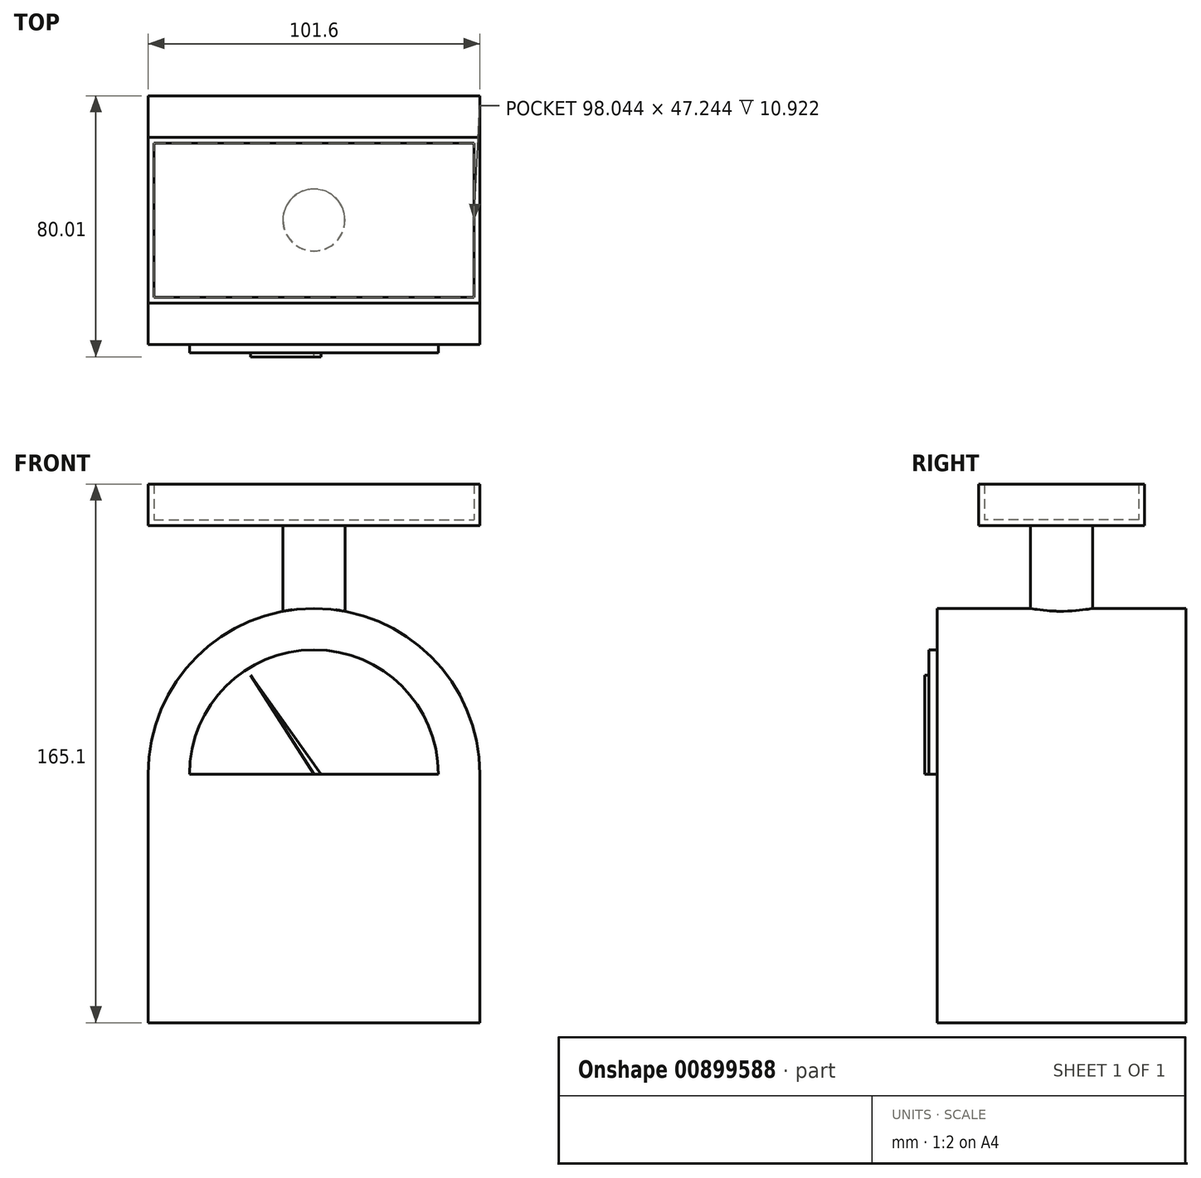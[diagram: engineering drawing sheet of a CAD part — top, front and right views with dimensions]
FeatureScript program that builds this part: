
annotation { "Feature Type Name" : "Feature", "Feature Type Description" : "" }
export const myFeature = defineFeature(function(context is Context, id is Id, definition is map)
    precondition{}
    {
        {
            var Q0;
            Q0=qCreatedBy(makeId("Front.planeOp"),FACE);
            var sketch = newSketch(context, id + "F0", { "sketchPlane" : qUnion([Q0])});
            skLineSegment(sketch, "E0", {"start": v(-50.8, 0) * mm, "end": v(50.8, 0) * mm});
            skLineSegment(sketch, "E1", {"start": v(50.8, 0) * mm, "end": v(50.8, 76.2) * mm});
            skLineSegment(sketch, "E2", {"start": v(-50.8, 0) * mm, "end": v(-50.8, 76.2) * mm});
            skArc(sketch, "E3", {"start": v(50.8, 76.2) * mm, "mid": v(0, 127) * mm, "end": v(-50.8, 76.2) * mm});
            skSolve(sketch);
        }
        {
            var Q0;
            Q0=makeQuery(id+"F0.imprint","IMPRINT",FACE,{"disambiguationData":[TD([[makeQuery(id+"F0.imprint","IMPRINT",EDGE,{"derivedFrom":sQuery(id+"F0.wireOp",EDGE,"E0")}),1.0]])]});
            extrude(context, id + "F1", {"entities" : qUnion([Q0]), "depth" : 76.2 * mm, "offsetDistance" : 25.4 * mm});
        }
        {
            var Q0;
            Q0=makeQuery(id+"F1.opExtrude","CAP_FACE",FACE,{"disambiguationData":[OSD([sQuery(id+"F0.wireOp",EDGE,"E0"),sQuery(id+"F0.wireOp",EDGE,"E1"),sQuery(id+"F0.wireOp",EDGE,"E2"),sQuery(id+"F0.wireOp",EDGE,"E3")])],"isStart":false});
            var sketch = newSketch(context, id + "F2", { "sketchPlane" : qUnion([Q0])});
            skLineSegment(sketch, "E4", {"start": v(-38.1, 76.2) * mm, "end": v(38.1, 76.2) * mm});
            skArc(sketch, "E5", {"start": v(38.1, 76.2) * mm, "mid": v(0, 114.3) * mm, "end": v(-38.1, 76.2) * mm});
            skSolve(sketch);
        }
        {
            var Q0;
            Q0=makeQuery(id+"F2.imprint","IMPRINT",FACE,{"disambiguationData":[TD([[makeQuery(id+"F2.imprint","IMPRINT",EDGE,{"derivedFrom":sQuery(id+"F2.wireOp",EDGE,"E4")}),1.0]])]});
            extrude(context, id + "F3", {"entities" : qUnion([Q0]), "depth" : 2.54 * mm, "offsetDistance" : 25.4 * mm});
        }
        {
            var Q0;
            Q0=makeQuery(id+"F3.opExtrude","CAP_FACE",FACE,{"disambiguationData":[OSD([sQuery(id+"F2.wireOp",EDGE,"E4"),sQuery(id+"F2.wireOp",EDGE,"E5")])],"isStart":false});
            var sketch = newSketch(context, id + "F4", { "sketchPlane" : qUnion([Q0])});
            skLineSegment(sketch, "E6", {"start": v(0, 76.2) * mm, "end": v(-19.35, 106.48) * mm});
            skLineSegment(sketch, "E7", {"start": v(-19.35, 106.48) * mm, "end": v(2.15, 76.2) * mm});
            skLineSegment(sketch, "E8", {"start": v(2.15, 76.2) * mm, "end": v(0, 76.2) * mm});
            skSolve(sketch);
        }
        {
            var Q0;
            Q0=makeQuery(id+"F4.imprint","IMPRINT",FACE,{"disambiguationData":[TD([[makeQuery(id+"F4.imprint","IMPRINT",EDGE,{"derivedFrom":sQuery(id+"F4.wireOp",EDGE,"E6")}),-1.0]])]});
            extrude(context, id + "F5", {"entities" : qUnion([Q0]), "depth" : 1.27 * mm, "offsetDistance" : 25.4 * mm});
        }
        {
            var Q0;
            Q0=qCreatedBy(makeId("Top.planeOp"),FACE);
            var sketch = newSketch(context, id + "F6", { "sketchPlane" : qUnion([Q0])});
            skCircle(sketch, "E9", {"center": v(0, -38.1) * mm, "radius": 9.53 * mm});
            skSolve(sketch);
        }
        {
            var Q0;
            Q0=makeQuery(id+"F6.imprint","IMPRINT",FACE,{"disambiguationData":[TD([[makeQuery(id+"F6.imprint","IMPRINT",EDGE,{"derivedFrom":sQuery(id+"F6.wireOp",EDGE,"E9")}),1.0]])]});
            extrude(context, id + "F7", {"entities" : qUnion([Q0]), "operationType" : NewBodyOperationType.ADD, "depth" : 152.4 * mm, "offsetDistance" : 25.4 * mm});
        }
        {
            var Q0;
            Q0=makeQuery(id+"F7.opExtrude","CAP_FACE",FACE,{"disambiguationData":[OSD([sQuery(id+"F6.wireOp",EDGE,"E9")])],"isStart":false});
            var sketch = newSketch(context, id + "F8", { "sketchPlane" : qUnion([Q0])});
            skLineSegment(sketch, "E10.bottom", {"start": v(-50.8, -12.7) * mm, "end": v(50.8, -12.7) * mm});
            skLineSegment(sketch, "E10.top", {"start": v(-50.8, -63.5) * mm, "end": v(50.8, -63.5) * mm});
            skLineSegment(sketch, "E10.left", {"start": v(-50.8, -12.7) * mm, "end": v(-50.8, -63.5) * mm});
            skLineSegment(sketch, "E10.right", {"start": v(50.8, -12.7) * mm, "end": v(50.8, -63.5) * mm});
            skSolve(sketch);
        }
        {
            var Q0;
            Q0=makeQuery(id+"F8.imprint","IMPRINT",FACE,{"disambiguationData":[TD([[makeQuery(id+"F8.imprint","IMPRINT",EDGE,{"derivedFrom":sQuery(id+"F8.wireOp",EDGE,"E10.bottom")}),-1.0]])]});
            var Q1;
            Q1=makeQuery(id+"F8.imprint","IMPRINT",FACE,{"disambiguationData":[TD([[makeQuery(id+"F8.imprint","IMPRINT",EDGE,{"derivedFrom":makeQuery(id+"F7.opExtrude","CAP_EDGE",EDGE,{"disambiguationData":[OSD([sQuery(id+"F6.wireOp",EDGE,"E9")])],"isStart":false})}),1.0]])]});
            extrude(context, id + "F9", {"entities" : qUnion([Q0, Q1]), "depth" : 12.7 * mm, "offsetDistance" : 25.4 * mm});
        }
        {
            var Q0;
            Q0=makeQuery(id+"F9.opExtrude","CAP_FACE",FACE,{"disambiguationData":[OSD([sQuery(id+"F8.wireOp",EDGE,"E10.bottom"),sQuery(id+"F8.wireOp",EDGE,"E10.top"),sQuery(id+"F8.wireOp",EDGE,"E10.left"),sQuery(id+"F8.wireOp",EDGE,"E10.right")])],"isStart":false});
            shell(context, id + "F10", {"entities" : qUnion([Q0]), "thickness" : 1.78 * mm});
        }
    });
